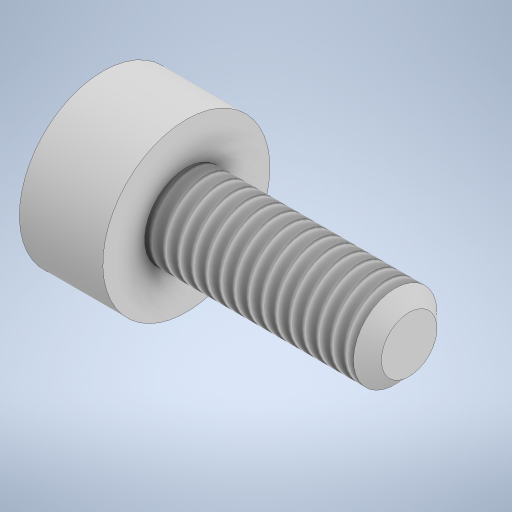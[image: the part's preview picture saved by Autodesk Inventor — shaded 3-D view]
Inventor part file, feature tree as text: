
AUTODESK INVENTOR PART (.ipt)
format: ipt  version: 2023 (Build 270158000, 158)  size: 273,920 bytes
history: native  units: mm
features: other x1, revolve x1, thread x1, chamfer x1, sketch x1
ambient origin geometry x8: Origin, YZ Plane, XZ Plane, XY Plane, X Axis, Y Axis, Z Axis, Center Point
bodies: Body1 (feature_tree)
feature tree (5):
  other  "Твердое тело1"
  revolve  "Вращение1"
  thread  "Резьба1"
  chamfer  "Фаска1"  Distance=3.0mm
  sketch  "Эскиз1"
